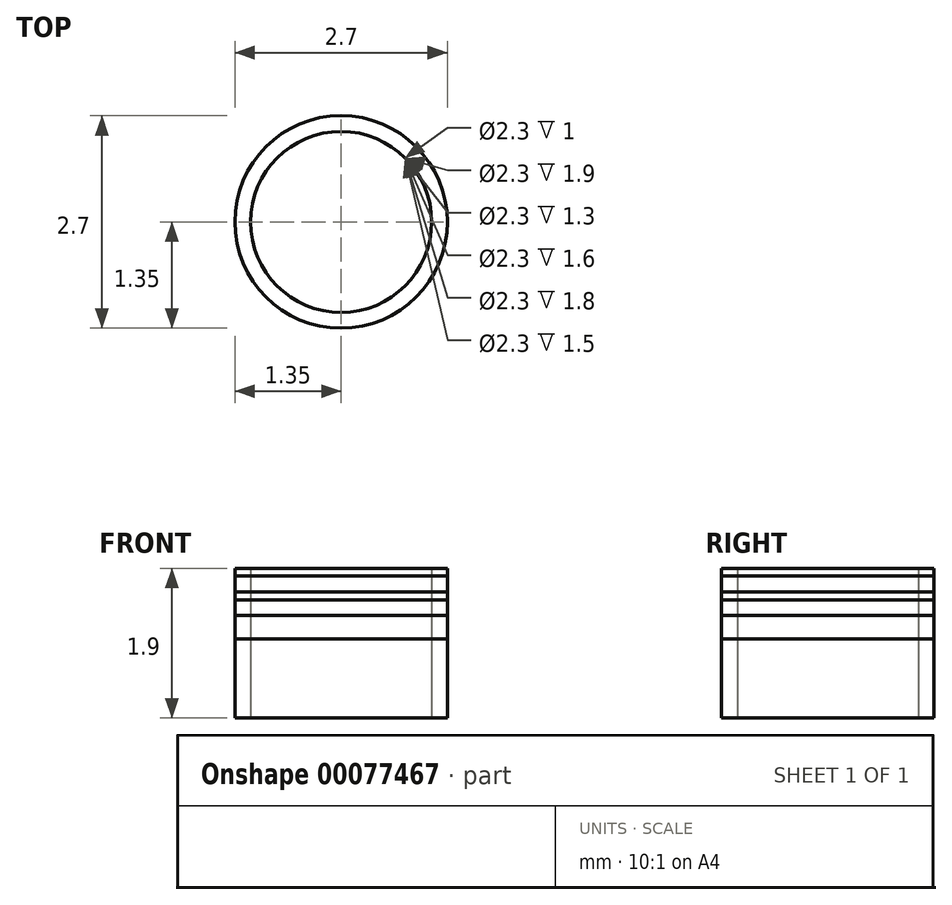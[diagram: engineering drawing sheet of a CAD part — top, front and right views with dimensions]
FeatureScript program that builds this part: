
annotation { "Feature Type Name" : "Feature", "Feature Type Description" : "" }
export const myFeature = defineFeature(function(context is Context, id is Id, definition is map)
    precondition{}
    {
        {
            var Q0;
            Q0=qCreatedBy(makeId("Top.planeOp"),FACE);
            var sketch = newSketch(context, id + "F0", { "sketchPlane" : qUnion([Q0])});
            skCircle(sketch, "E0", {"center": v(0, 0) * mm, "radius": 1.35 * mm});
            skCircle(sketch, "E1", {"center": v(0, 0) * mm, "radius": 1.15 * mm});
            skSolve(sketch);
        }
        {
            var Q0;
            Q0=makeQuery(id+"F0.imprint","IMPRINT",FACE,{"disambiguationData":[TD([[makeQuery(id+"F0.imprint","IMPRINT",EDGE,{"derivedFrom":sQuery(id+"F0.wireOp",EDGE,"E0")}),1.0]])]});
            extrude(context, id + "F1", {"entities" : qUnion([Q0]), "depth" : 1.5 * mm});
        }
        {
            var Q0;
            Q0=makeQuery(id+"F0.imprint","IMPRINT",FACE,{"disambiguationData":[TD([[makeQuery(id+"F0.imprint","IMPRINT",EDGE,{"derivedFrom":sQuery(id+"F0.wireOp",EDGE,"E0")}),1.0]])]});
            extrude(context, id + "F2", {"entities" : qUnion([Q0]), "depth" : 1.6 * mm});
        }
        {
            var Q0;
            Q0=makeQuery(id+"F0.imprint","IMPRINT",FACE,{"disambiguationData":[TD([[makeQuery(id+"F0.imprint","IMPRINT",EDGE,{"derivedFrom":sQuery(id+"F0.wireOp",EDGE,"E0")}),1.0]])]});
            extrude(context, id + "F3", {"entities" : qUnion([Q0]), "depth" : 1.8 * mm});
        }
        {
            var Q0;
            Q0=makeQuery(id+"F0.imprint","IMPRINT",FACE,{"disambiguationData":[TD([[makeQuery(id+"F0.imprint","IMPRINT",EDGE,{"derivedFrom":sQuery(id+"F0.wireOp",EDGE,"E0")}),1.0]])]});
            extrude(context, id + "F4", {"entities" : qUnion([Q0]), "depth" : 1.9 * mm});
        }
        {
            var Q0;
            Q0=makeQuery(id+"F0.imprint","IMPRINT",FACE,{"disambiguationData":[TD([[makeQuery(id+"F0.imprint","IMPRINT",EDGE,{"derivedFrom":sQuery(id+"F0.wireOp",EDGE,"E0")}),1.0]])]});
            extrude(context, id + "F5", {"entities" : qUnion([Q0]), "depth" : 1.3 * mm});
        }
        {
            var Q0;
            Q0=makeQuery(id+"F0.imprint","IMPRINT",FACE,{"disambiguationData":[TD([[makeQuery(id+"F0.imprint","IMPRINT",EDGE,{"derivedFrom":sQuery(id+"F0.wireOp",EDGE,"E0")}),1.0]])]});
            extrude(context, id + "F6", {"entities" : qUnion([Q0]), "depth" : 1 * mm});
        }
    });
